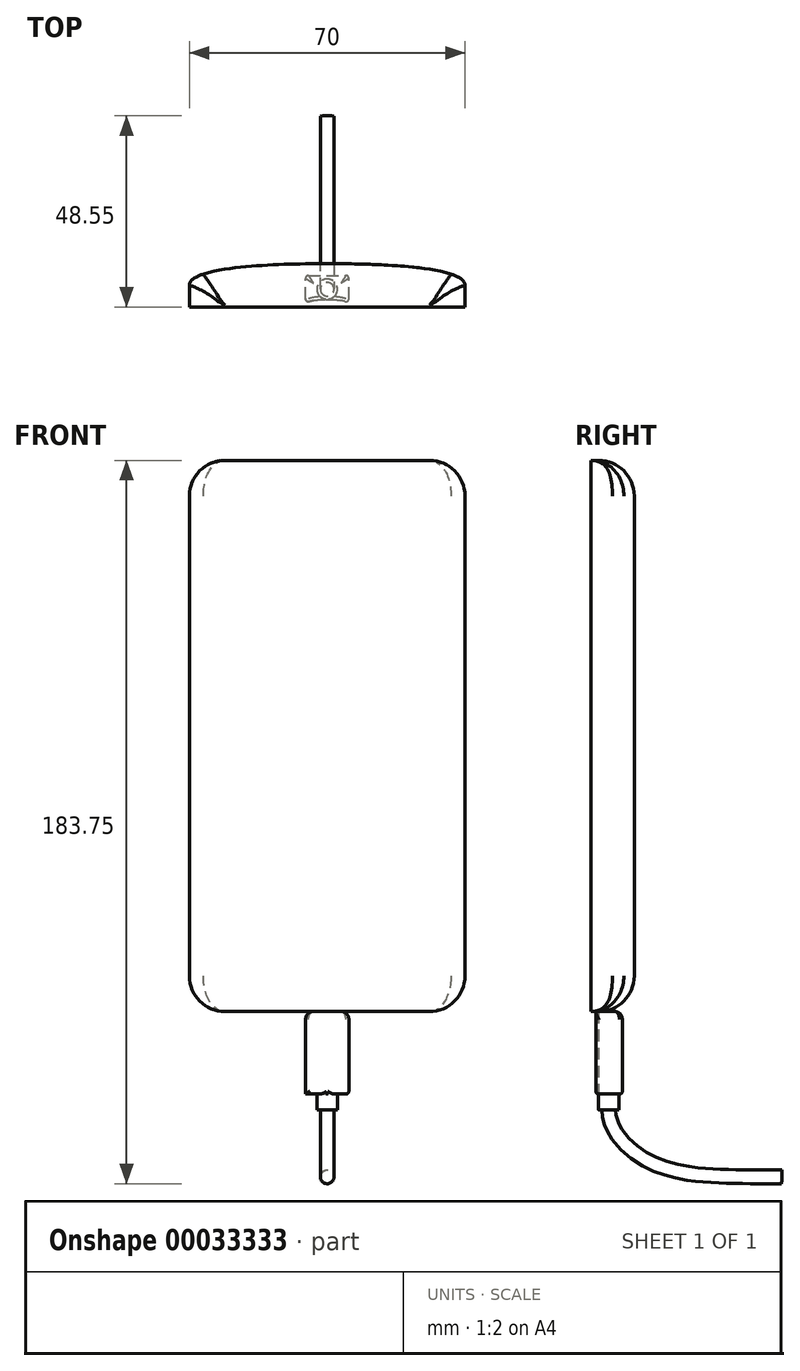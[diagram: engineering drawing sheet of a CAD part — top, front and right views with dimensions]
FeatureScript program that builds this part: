
annotation { "Feature Type Name" : "Feature", "Feature Type Description" : "" }
export const myFeature = defineFeature(function(context is Context, id is Id, definition is map)
    precondition{}
    {
        {
            var Q0;
            Q0=qCreatedBy(makeId("Front.planeOp"),FACE);
            var sketch = newSketch(context, id + "F0", { "sketchPlane" : qUnion([Q0])});
            skLineSegment(sketch, "E0.bottom", {"start": v(-35, 140) * mm, "end": v(35, 140) * mm});
            skLineSegment(sketch, "E0.top", {"start": v(-35, 0) * mm, "end": v(35, 0) * mm});
            skLineSegment(sketch, "E0.left", {"start": v(-35, 140) * mm, "end": v(-35, 0) * mm});
            skLineSegment(sketch, "E0.right", {"start": v(35, 140) * mm, "end": v(35, 0) * mm});
            skSolve(sketch);
        }
        {
            var Q0;
            Q0 = qSketchRegion(id + "F0", true);
            extrude(context, id + "F1", {"entities" : qUnion([Q0]), "depth" : 11 * mm});
        }
        {
            var Q0;
            Q0=makeQuery(id+"F1.opExtrude","SWEPT_FACE",FACE,{"disambiguationData":[OSD([sQuery(id+"F0.wireOp",EDGE,"E0.bottom")])]});
            var sketch = newSketch(context, id + "F2", { "sketchPlane" : qUnion([Q0])});
            skFitSpline(sketch, "E1", {"points": [v(-35, -5.5) * mm, v(0, 0) * mm], "startDerivative": vector(0, 16.5) * mm, "endDerivative": vector(18.96, 0) * mm});
            skFitSpline(sketch, "E2.MirrorCS", {"points": [v(35, -5.5) * mm, v(0, 0) * mm], "startDerivative": vector(0, 16.5) * mm, "endDerivative": vector(-18.96, 0) * mm});
            skLineSegment(sketch, "E3", {"start": v(-35, -5.5) * mm, "end": v(-35, 11.17) * mm});
            skLineSegment(sketch, "E4", {"start": v(35, -5.5) * mm, "end": v(35, 11.17) * mm});
            skLineSegment(sketch, "E5", {"start": v(35, 11.17) * mm, "end": v(-35, 11.17) * mm});
            skSolve(sketch);
        }
        {
            var Q0;
            Q0 = qSketchRegion(id + "F2", true);
            extrude(context, id + "F3", {"entities" : qUnion([Q0]), "operationType" : NewBodyOperationType.REMOVE, "endBound" : BoundingType.THROUGH_ALL, "oppositeDirection" : true, "depth" : 25 * mm});
        }
        {
            var Q0;
            Q0=makeQuery(id+"F1.opExtrude","SWEPT_EDGE",EDGE,{"disambiguationData":[OSD([sQuery(id+"F0.wireOp",EDGE,"E0.bottom"),sQuery(id+"F0.wireOp",EDGE,"E0.left")])]});
            var Q1;
            Q1=makeQuery(id+"F1.opExtrude","SWEPT_EDGE",EDGE,{"disambiguationData":[OSD([sQuery(id+"F0.wireOp",EDGE,"E0.top"),sQuery(id+"F0.wireOp",EDGE,"E0.left")])]});
            var Q2;
            Q2=makeQuery(id+"F1.opExtrude","SWEPT_EDGE",EDGE,{"disambiguationData":[OSD([sQuery(id+"F0.wireOp",EDGE,"E0.top"),sQuery(id+"F0.wireOp",EDGE,"E0.right")])]});
            var Q3;
            Q3=makeQuery(id+"F1.opExtrude","SWEPT_EDGE",EDGE,{"disambiguationData":[OSD([sQuery(id+"F0.wireOp",EDGE,"E0.bottom"),sQuery(id+"F0.wireOp",EDGE,"E0.right")])]});
            fillet(context, id + "F4", {"entities" : qUnion([Q0, Q1, Q2, Q3]), "radius" : 9 * mm, "tangentPropagation" : true, "allowEdgeOverflow" : false});
        }
        {
            var Q0;
            Q0=qCreatedBy(makeId("Top.planeOp"),FACE);
            var sketch = newSketch(context, id + "F5", { "sketchPlane" : qUnion([Q0])});
            skLineSegment(sketch, "E6.top", {"start": v(-5.5, -3) * mm, "end": v(5.5, -3) * mm});
            skLineSegment(sketch, "E6.left", {"start": v(-5.5, -10) * mm, "end": v(-5.5, -3) * mm});
            skLineSegment(sketch, "E6.right", {"start": v(5.5, -10) * mm, "end": v(5.5, -3) * mm});
            skPoint(sketch, "E7.1.internal.snap0", {"position": v(0, -10) * mm});
            skFitSpline(sketch, "E7", {"points": [v(-5.5, -10) * mm, v(0, -9.09) * mm, v(5.5, -10) * mm], "startDerivative": vector(11, 4.91) * mm, "endDerivative": vector(11, -4.91) * mm});
            skSolve(sketch);
        }
        {
            var Q0;
            Q0 = qSketchRegion(id + "F5", true);
            extrude(context, id + "F6", {"entities" : qUnion([Q0]), "oppositeDirection" : true, "depth" : 21 * mm});
        }
        {
            var Q0;
            Q0=makeQuery(id+"F6.opExtrude","CAP_FACE",FACE,{"disambiguationData":[OSD([sQuery(id+"F5.wireOp",EDGE,"E6.top"),sQuery(id+"F5.wireOp",EDGE,"E6.left"),sQuery(id+"F5.wireOp",EDGE,"E6.right"),sQuery(id+"F5.wireOp",EDGE,"E7")])],"isStart":false});
            var sketch = newSketch(context, id + "F7", { "sketchPlane" : qUnion([Q0])});
            skLineSegment(sketch, "E8", {"start": v(5.5, 10) * mm, "end": v(-5.5, 3) * mm, "construction": true});
            skLineSegment(sketch, "E9", {"start": v(-5.5, 10) * mm, "end": v(5.5, 3) * mm, "construction": true});
            skCircle(sketch, "E10", {"center": v(0, 6.5) * mm, "radius": 2.6 * mm});
            skSolve(sketch);
        }
        {
            var Q0;
            Q0 = qSketchRegion(id + "F7", true);
            extrude(context, id + "F8", {"entities" : qUnion([Q0]), "operationType" : NewBodyOperationType.ADD, "depth" : 4 * mm});
        }
        {
            var Q0;
            Q0=qCreatedBy(makeId("Right.planeOp"),FACE);
            var sketch = newSketch(context, id + "F9", { "sketchPlane" : qUnion([Q0])});
            skLineSegment(sketch, "E11.bottom", {"start": v(-6.5, -25) * mm, "end": v(37.5, -25) * mm, "construction": true});
            skLineSegment(sketch, "E11.top", {"start": v(-6.5, -42) * mm, "end": v(37.5, -42) * mm, "construction": true});
            skLineSegment(sketch, "E11.left", {"start": v(-6.5, -25) * mm, "end": v(-6.5, -42) * mm, "construction": true});
            skLineSegment(sketch, "E11.right", {"start": v(37.5, -25) * mm, "end": v(37.5, -42) * mm, "construction": true});
            skFitSpline(sketch, "E12", {"points": [v(-6.5, -25) * mm, v(4.01, -38.24) * mm, v(37.5, -42) * mm], "startDerivative": vector(1.17, -39.65) * mm, "endDerivative": vector(78.42, 0) * mm});
            skSolve(sketch);
        }
        {
            var Q0;
            Q0=makeQuery(id+"F8.opExtrude","CAP_FACE",FACE,{"disambiguationData":[OSD([sQuery(id+"F7.wireOp",EDGE,"E10")])],"isStart":false});
            var sketch = newSketch(context, id + "F10", { "sketchPlane" : qUnion([Q0])});
            skCircle(sketch, "E13", {"center": v(0, 6.5) * mm, "radius": 1.75 * mm});
            skSolve(sketch);
        }
        {
            var Q0;
            Q0=makeQuery(id+"F10.imprint","IMPRINT",FACE,{"disambiguationData":[TD([[makeQuery(id+"F10.imprint","IMPRINT",EDGE,{"derivedFrom":sQuery(id+"F10.wireOp",EDGE,"E13")}),1.0]])]});
            var Q1;
            Q1=sQuery(id+"F9.wireOp",EDGE,"E12");
            sweep(context, id + "F11", {"operationType" : NewBodyOperationType.ADD, "profiles" : qUnion([Q0]), "path" : qUnion([Q1])});
        }
        {
            var Q0;
            Q0=makeQuery(id+"F6.opExtrude","SWEPT_EDGE",EDGE,{"disambiguationData":[OSD([sQuery(id+"F5.wireOp",EDGE,"E6.left"),sQuery(id+"F5.wireOp",EDGE,"E7")])]});
            var Q1;
            Q1=makeQuery(id+"F6.opExtrude","SWEPT_EDGE",EDGE,{"disambiguationData":[OSD([sQuery(id+"F5.wireOp",EDGE,"E6.right"),sQuery(id+"F5.wireOp",EDGE,"E7")])]});
            var Q2;
            Q2=makeQuery(id+"F6.opExtrude","SWEPT_EDGE",EDGE,{"disambiguationData":[OSD([sQuery(id+"F5.wireOp",EDGE,"E6.top"),sQuery(id+"F5.wireOp",EDGE,"E6.right")])]});
            var Q3;
            Q3=makeQuery(id+"F6.opExtrude","SWEPT_EDGE",EDGE,{"disambiguationData":[OSD([sQuery(id+"F5.wireOp",EDGE,"E6.top"),sQuery(id+"F5.wireOp",EDGE,"E6.left")])]});
            var Q4;
            Q4=makeQuery(id+"F6.opExtrude","CAP_EDGE",EDGE,{"disambiguationData":[OSD([sQuery(id+"F5.wireOp",EDGE,"E6.right")])],"isStart":false});
            var Q5;
            {var subQ0=sQuery(id+"F5.wireOp",EDGE,"E7");var subQ1=sQuery(id+"F7.wireOp",EDGE,"E10");var subQ2=sQuery(id+"F5.wireOp",EDGE,"E6.right");Q5=makeQuery(id+"F8.boolean.opBoolean","SPLIT",EDGE,{"disambiguationData":[TD([makeQuery(id+"F6.opExtrude","CAP_FACE",FACE,{"disambiguationData":[OSD([sQuery(id+"F5.wireOp",EDGE,"E6.top"),sQuery(id+"F5.wireOp",EDGE,"E6.left"),subQ2,subQ0])],"isStart":false}),makeQuery(id+"F6.opExtrude","SWEPT_FACE",FACE,{"disambiguationData":[OSD([subQ2])]}),makeQuery(id+"F6.opExtrude","SWEPT_FACE",FACE,{"disambiguationData":[OSD([subQ0])]}),makeQuery(id+"F8.opExtrude","SWEPT_FACE",FACE,{"disambiguationData":[OSD([subQ1])]}),makeQuery(id+"F8.opExtrude","CAP_FACE",FACE,{"disambiguationData":[OSD([subQ1])],"isStart":true})])],"derivedFrom":makeQuery(id+"F6.opExtrude","CAP_EDGE",EDGE,{"disambiguationData":[OSD([subQ0])],"isStart":false})});}
            var Q6;
            {var subQ0=sQuery(id+"F5.wireOp",EDGE,"E7");var subQ1=sQuery(id+"F7.wireOp",EDGE,"E10");var subQ2=sQuery(id+"F5.wireOp",EDGE,"E6.left");Q6=makeQuery(id+"F8.boolean.opBoolean","SPLIT",EDGE,{"disambiguationData":[TD([makeQuery(id+"F6.opExtrude","CAP_FACE",FACE,{"disambiguationData":[OSD([sQuery(id+"F5.wireOp",EDGE,"E6.top"),subQ2,sQuery(id+"F5.wireOp",EDGE,"E6.right"),subQ0])],"isStart":false}),makeQuery(id+"F6.opExtrude","SWEPT_FACE",FACE,{"disambiguationData":[OSD([subQ2])]}),makeQuery(id+"F6.opExtrude","SWEPT_FACE",FACE,{"disambiguationData":[OSD([subQ0])]}),makeQuery(id+"F8.opExtrude","SWEPT_FACE",FACE,{"disambiguationData":[OSD([subQ1])]}),makeQuery(id+"F8.opExtrude","CAP_FACE",FACE,{"disambiguationData":[OSD([subQ1])],"isStart":true})])],"derivedFrom":makeQuery(id+"F6.opExtrude","CAP_EDGE",EDGE,{"disambiguationData":[OSD([subQ0])],"isStart":false})});}
            var Q7;
            Q7=makeQuery(id+"F6.opExtrude","CAP_EDGE",EDGE,{"disambiguationData":[OSD([sQuery(id+"F5.wireOp",EDGE,"E6.top")])],"isStart":false});
            fillet(context, id + "F12", {"entities" : qUnion([Q0, Q1, Q2, Q3, Q4, Q5, Q6, Q7]), "radius" : 0.75 * mm, "tangentPropagation" : true, "allowEdgeOverflow" : false});
        }
        {
            var Q0;
            Q0=makeQuery(id+"F6.opExtrude","CAP_EDGE",EDGE,{"disambiguationData":[OSD([sQuery(id+"F5.wireOp",EDGE,"E6.top")])],"isStart":true});
            var Q1;
            Q1=makeQuery(id+"F6.opExtrude","CAP_EDGE",EDGE,{"disambiguationData":[OSD([sQuery(id+"F5.wireOp",EDGE,"E6.right")])],"isStart":true});
            var Q2;
            Q2=makeQuery(id+"F6.opExtrude","CAP_EDGE",EDGE,{"disambiguationData":[OSD([sQuery(id+"F5.wireOp",EDGE,"E6.left")])],"isStart":true});
            fillet(context, id + "F13", {"entities" : qUnion([Q0, Q1, Q2]), "radius" : 2 * mm, "allowEdgeOverflow" : false});
        }
    });
